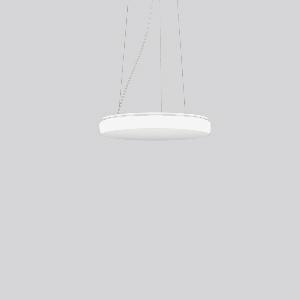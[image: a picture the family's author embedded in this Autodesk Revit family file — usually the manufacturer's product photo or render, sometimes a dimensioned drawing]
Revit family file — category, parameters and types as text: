
# Revit family: flat_polymero_kreis_slim_312241_002_1_8d0f
name_source: partatom
category: Lighting Fixtures
units: mm (PartAtom-declared; Revit-internal decimal feet)

## family parameters
Cut with Voids When Loaded = No
Host = Face
Light Source = No
Part Type = Normal
Room Calculation Point = No
Round Connector Dimension = Use Diameter
Shared = No

## types (1)
- FLAT POLYMERO KREIS SLIM (1 x LED Modul 830, 2600 lm, 3000)
    Apparent Load = 24 VA
    CIE Flux Codes = 41 72 91 83 100
    Color Rendering = 80
    Color Temperature = 3000
    Default Elevation = 1800 mm
    Description = Series: FLAT POLYMERO KREIS SLIM
Decorative round LED pendant luminaire. Base and canopy: metal, powder-coated, white. Canopy Ø 205 mm, h 35 mm. Diffuser made of non-yellowing plastic (PMMA), opal. Diffuser fastening: patented push system. Homogeneous and smooth light distribution. Suitable for pendant. 3-point steel cable suspension, steplessly adjustable. Special lengths available on request. 
Colour: white
Diameter: 460 mm
Height: 68 mm
Suspension length: 200-1300 mm
Lamp: LED exchangeable
Socket: without socket
Colour temperature: 3000K
Colour rendering index (CRI): 83
System power: 24 W
Rated luminous flux: 2600 lm
Luminous efficiency: 108 lm/W
Control gear: AC Strom, dim.Ph.an-/abschnitt
Protection class: I
Type of protection: IP 40
    Height = 68 mm
    Lamp = 1 x LED Modul 830
    Lamp Light Flux = 2600 lm
    Lamp count = 1
    Length = 460 mm
    Lifetime = 50000 h
    Luminous efficacy = 108 lm/W
    Manufacturer = RZB
    ModVariant = No
    Model = 312241.002.1
    Mounting Place = Ceiling
    Mounting Type = Pendant
    Number of Poles = 1
    OnlyDefault = Yes
    Power Factor = 1
    Product Name = FLAT POLYMERO KREIS SLIM
    Product group = Pendant luminaires
    ProductGroupID = 902
    Protection Class = Protection class I
    Protection Degree = IP 40
    RLX_Detail_Level = 1
    RLX_Emergency_Light_Flux = 0 lm
    RLX_Emergency_Type = 0
    RLX_Emergency_Type_DB = No
    RlxData = <blob elided: 58033 chars, md5=188b50c8>
    Socket = socket
    Standby Power = 0 W
    System Light Flux = 2600 lm
    System Power = 24 W
    Type Comments = Product without accessories
    Type Image = 312090.002.jpg
    URL = http://relux.com
    VarID = ---
    Voltage = 230 V
    Voltage Range = 220-240 V
    Weight = 0.00 kg
    Width = 0 mm  [stored 0 ft]

note: [stored X ft] marks values corroborated as IEEE doubles in the binary element streams (Revit-internal decimal feet)

## geometry (parser evidence)
native form markers: Blend x4, Sweep x13
no freeform markers — native parametric forms only
